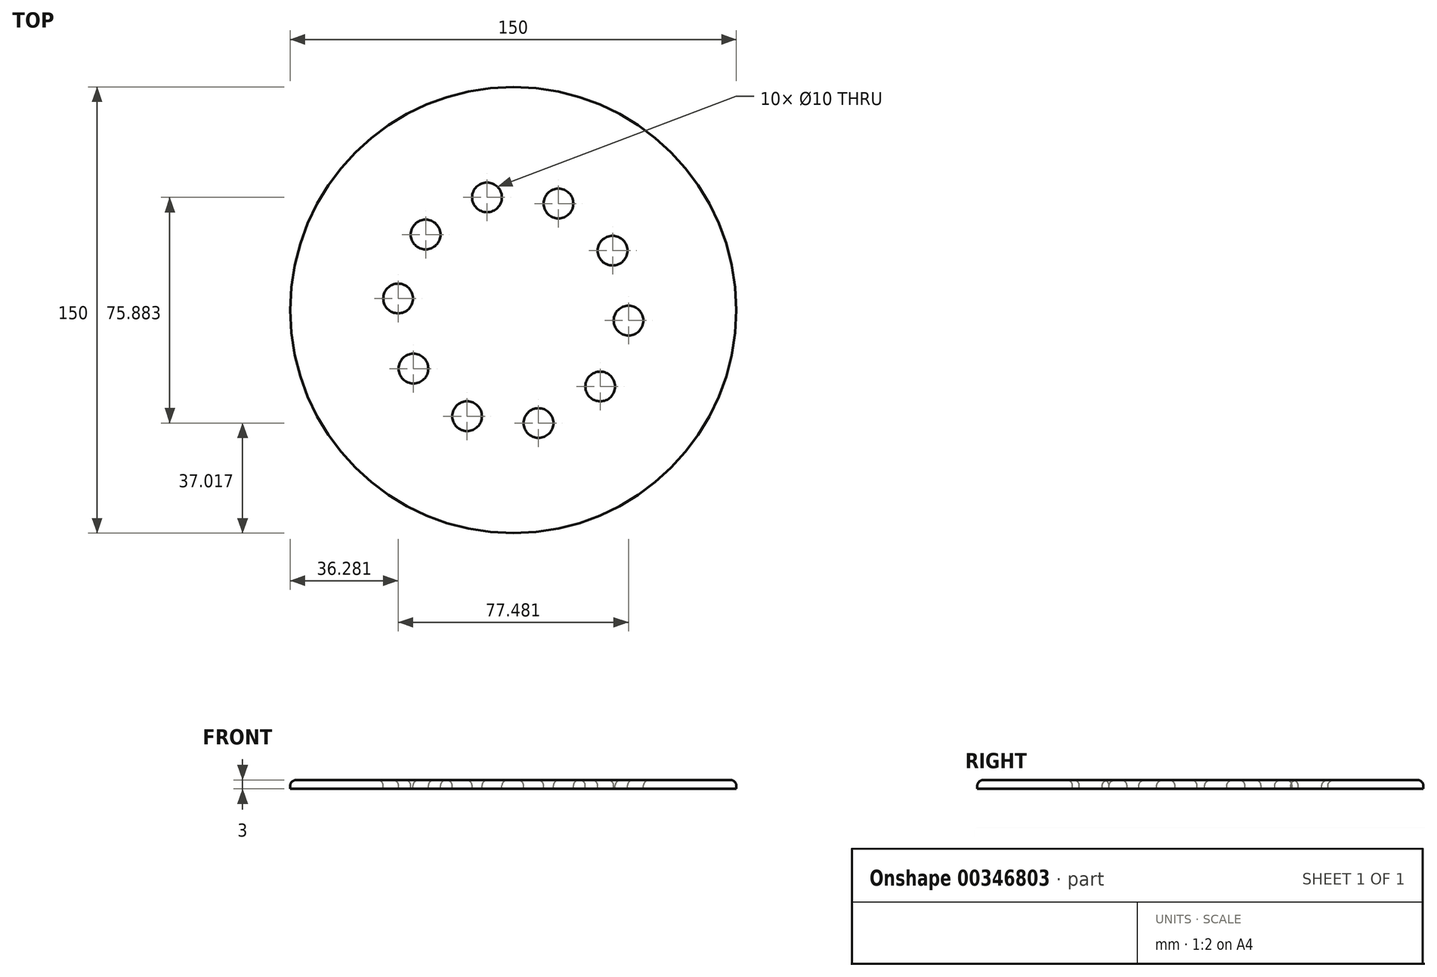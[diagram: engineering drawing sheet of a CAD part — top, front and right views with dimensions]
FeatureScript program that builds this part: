
annotation { "Feature Type Name" : "Feature", "Feature Type Description" : "" }
export const myFeature = defineFeature(function(context is Context, id is Id, definition is map)
    precondition{}
    {
        {
            var Q0;
            Q0=qCreatedBy(makeId("Top.planeOp"),FACE);
            var sketch = newSketch(context, id + "F0", { "sketchPlane" : qUnion([Q0])});
            skCircle(sketch, "E0", {"center": v(-21.46, 5.64) * mm, "radius": 75 * mm});
            skSolve(sketch);
        }
        {
            var Q0;
            Q0=makeQuery(id+"F0.imprint","IMPRINT",FACE,{"disambiguationData":[TD([[makeQuery(id+"F0.imprint","IMPRINT",EDGE,{"derivedFrom":sQuery(id+"F0.wireOp",EDGE,"E0")}),1.0]])]});
            extrude(context, id + "F1", {"entities" : qUnion([Q0]), "depth" : 3 * mm});
        }
        {
            var Q0;
            Q0=makeQuery(id+"F1.opExtrude","CAP_FACE",FACE,{"disambiguationData":[OSD([sQuery(id+"F0.wireOp",EDGE,"E0")])],"isStart":false});
            var sketch = newSketch(context, id + "F2", { "sketchPlane" : qUnion([Q0])});
            skCircle(sketch, "E1", {"center": v(-50.94, 31.04) * mm, "radius": 5 * mm});
            skCircle(sketch, "E2.1.0", {"center": v(-30.3, 43.54) * mm, "radius": 5 * mm});
            skCircle(sketch, "E2.2.0", {"center": v(-6.27, 41.47) * mm, "radius": 5 * mm});
            skCircle(sketch, "E2.3.0", {"center": v(11.93, 25.64) * mm, "radius": 5 * mm});
            skCircle(sketch, "E2.4.0", {"center": v(17.3, 2.12) * mm, "radius": 5 * mm});
            skCircle(sketch, "E2.5.0", {"center": v(7.78, -20.05) * mm, "radius": 5 * mm});
            skCircle(sketch, "E2.6.0", {"center": v(-12.98, -32.34) * mm, "radius": 5 * mm});
            skCircle(sketch, "E2.7.0", {"center": v(-37, -30.04) * mm, "radius": 5 * mm});
            skCircle(sketch, "E2.8.0", {"center": v(-55.04, -14.03) * mm, "radius": 5 * mm});
            skCircle(sketch, "E2.9.0", {"center": v(-60.18, 9.54) * mm, "radius": 5 * mm});
            skPoint(sketch, "E2.center", {"position": v(-21.46, 5.64) * mm});
            skLineSegment(sketch, "E2.anchor1", {"start": v(-21.46, 5.64) * mm, "end": v(-50.94, 31.04) * mm, "construction": true});
            skLineSegment(sketch, "E2.anchor2", {"start": v(-21.46, 5.64) * mm, "end": v(-60.18, 9.54) * mm, "construction": true});
            skSolve(sketch);
        }
        {
            var Q0;
            Q0=sQuery(id+"F2.wireOp",VERTEX,"E1.center");
            var Q1;
            Q1=sQuery(id+"F2.wireOp",VERTEX,"E2.1.0.center");
            var Q2;
            Q2=sQuery(id+"F2.wireOp",VERTEX,"E2.2.0.center");
            var Q3;
            Q3=sQuery(id+"F2.wireOp",VERTEX,"E2.3.0.center");
            var Q4;
            Q4=sQuery(id+"F2.wireOp",VERTEX,"E2.4.0.center");
            var Q5;
            Q5=sQuery(id+"F2.wireOp",VERTEX,"E2.5.0.center");
            var Q6;
            Q6=sQuery(id+"F2.wireOp",VERTEX,"E2.6.0.center");
            var Q7;
            Q7=sQuery(id+"F2.wireOp",VERTEX,"E2.7.0.center");
            var Q8;
            Q8=sQuery(id+"F2.wireOp",VERTEX,"E2.8.0.center");
            var Q9;
            Q9=sQuery(id+"F2.wireOp",VERTEX,"E2.anchor2.end");
            var Q10;
            Q10=makeQuery(id+"F1.opExtrude","SWEPT_BODY",BODY,{"disambiguationData":[OSD([sQuery(id+"F0.wireOp",EDGE,"E0")])]});
            hole(context, id + "F3", {"style" : HoleStyle.SIMPLE, "endStyle" : HoleEndStyle.THROUGH, "holeDiameter" : 10 * mm, "isTappedThrough" : true, "tappedDepth" : 12 * mm, "tapClearance" : 3, "locations" : qUnion([Q0, Q1, Q2, Q3, Q4, Q5, Q6, Q7, Q8, Q9]), "scope" : qUnion([Q10])});
        }
        {
            var Q0;
            Q0=makeQuery(id+"F1.opExtrude","CAP_FACE",FACE,{"disambiguationData":[OSD([sQuery(id+"F0.wireOp",EDGE,"E0")])],"isStart":false});
            fillet(context, id + "F4", {"entities" : qUnion([Q0]), "radius" : 2 * mm, "tangentPropagation" : true, "allowEdgeOverflow" : false});
        }
    });
